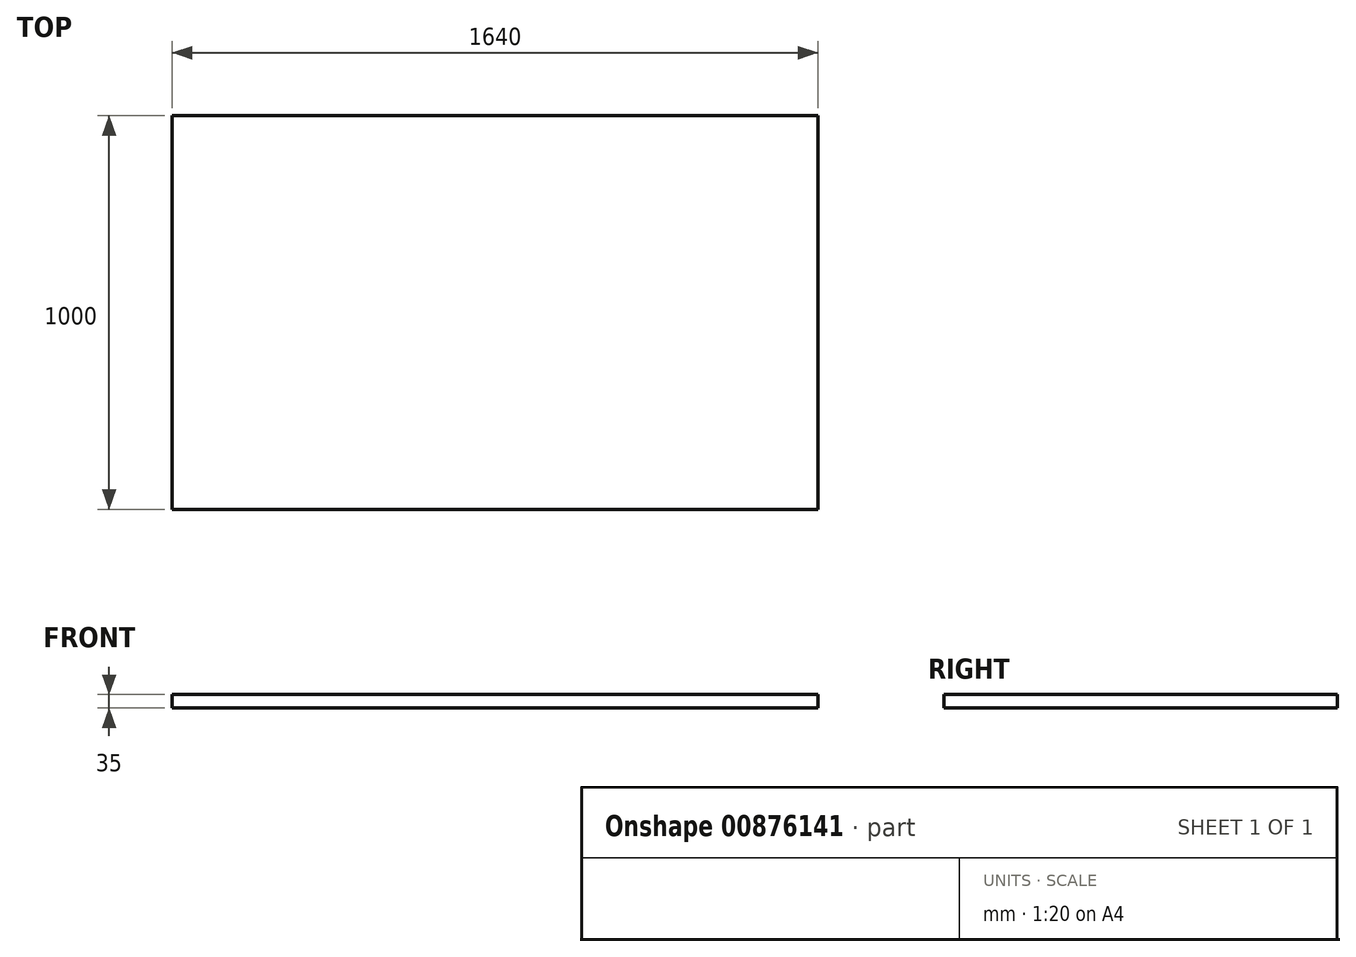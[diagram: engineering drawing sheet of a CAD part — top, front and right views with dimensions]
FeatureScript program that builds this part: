
annotation { "Feature Type Name" : "Feature", "Feature Type Description" : "" }
export const myFeature = defineFeature(function(context is Context, id is Id, definition is map)
    precondition{}
    {
        {
            var Q0;
            Q0=qCreatedBy(makeId("Front.planeOp"),FACE);
            var sketch = newSketch(context, id + "F0", { "sketchPlane" : qUnion([Q0])});
            skLineSegment(sketch, "E0.bottom", {"start": v(-168.33, 0) * mm, "end": v(1471.67, 0) * mm});
            skLineSegment(sketch, "E0.top", {"start": v(-168.33, 35) * mm, "end": v(1471.67, 35) * mm});
            skLineSegment(sketch, "E0.left", {"start": v(-168.33, 0) * mm, "end": v(-168.33, 35) * mm});
            skLineSegment(sketch, "E0.right", {"start": v(1471.67, 0) * mm, "end": v(1471.67, 35) * mm});
            skSolve(sketch);
        }
        {
            var Q0;
            Q0=makeQuery(id+"F0.imprint","IMPRINT",FACE,{"disambiguationData":[TD([[makeQuery(id+"F0.imprint","IMPRINT",EDGE,{"derivedFrom":sQuery(id+"F0.wireOp",EDGE,"E0.bottom")}),1.0]])]});
            extrude(context, id + "F1", {"entities" : qUnion([Q0]), "depth" : 1000 * mm, "offsetDistance" : 25 * mm});
        }
    });
